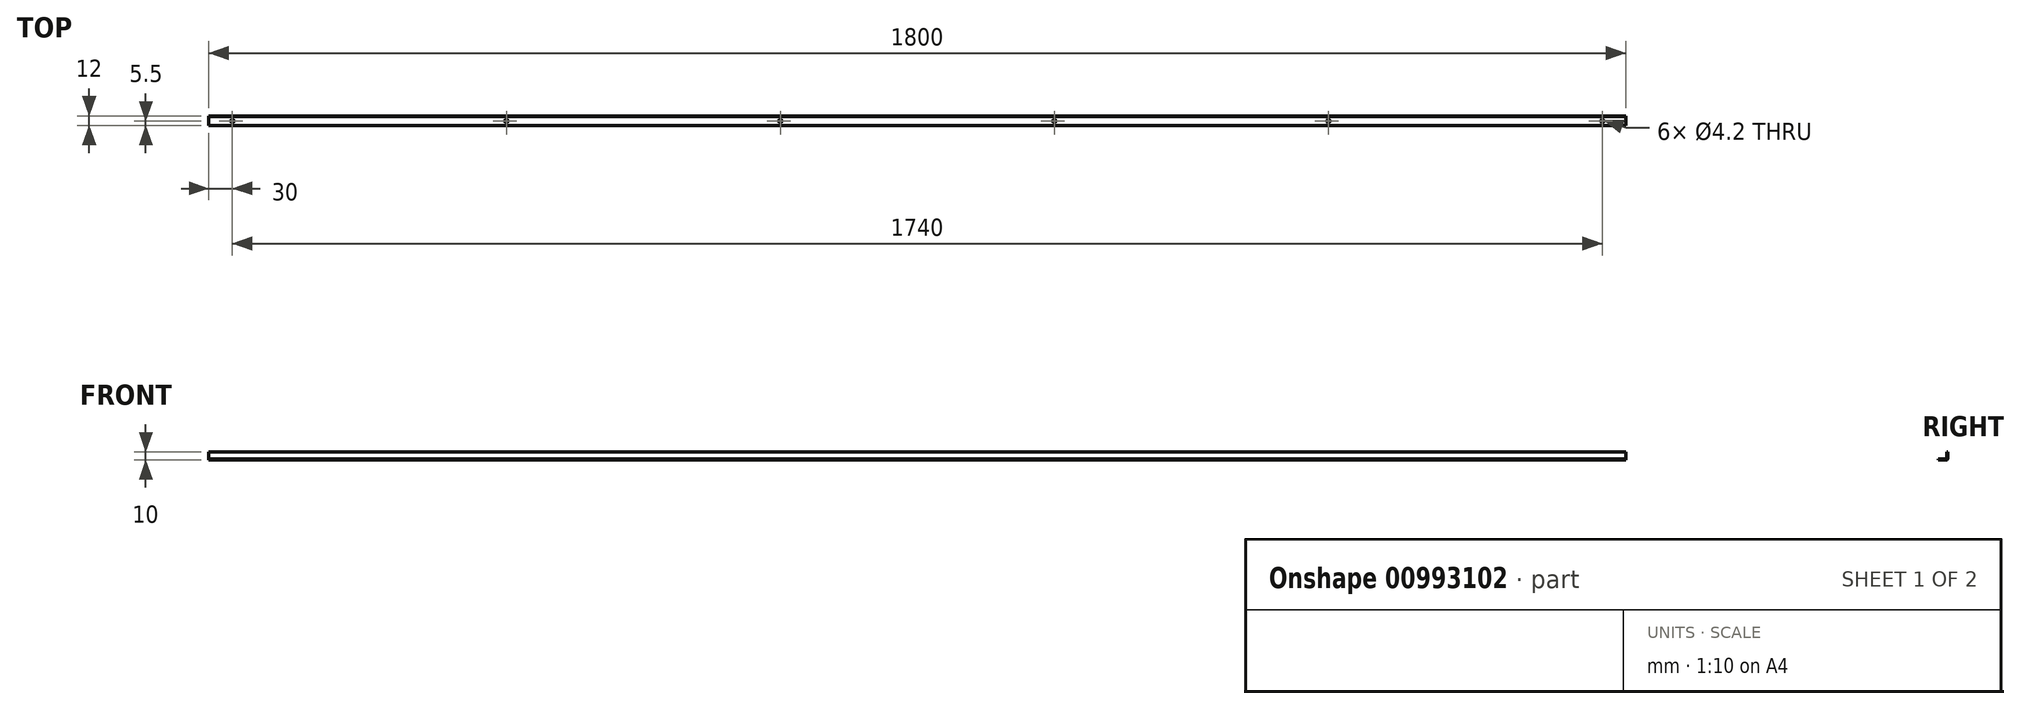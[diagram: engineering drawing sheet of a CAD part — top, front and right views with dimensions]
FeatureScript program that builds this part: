
annotation { "Feature Type Name" : "Feature", "Feature Type Description" : "" }
export const myFeature = defineFeature(function(context is Context, id is Id, definition is map)
    precondition{}
    {
        {
            var Q0;
            Q0=qCreatedBy(makeId("Right.planeOp"),FACE);
            var sketch = newSketch(context, id + "F0", { "sketchPlane" : qUnion([Q0])});
            skLineSegment(sketch, "E0", {"start": v(0, 0) * mm, "end": v(0, 10) * mm});
            skLineSegment(sketch, "E1", {"start": v(0, 10) * mm, "end": v(-1, 10) * mm});
            skLineSegment(sketch, "E2", {"start": v(-1, 10) * mm, "end": v(-1, 1) * mm});
            skLineSegment(sketch, "E3", {"start": v(-1, 1) * mm, "end": v(-12, 1) * mm});
            skLineSegment(sketch, "E4", {"start": v(-12, 1) * mm, "end": v(-12, 0) * mm});
            skLineSegment(sketch, "E5", {"start": v(-12, 0) * mm, "end": v(0, 0) * mm});
            skSolve(sketch);
        }
        {
            var Q0;
            Q0 = qSketchRegion(id + "F0", true);
            extrude(context, id + "F1", {"entities" : qUnion([Q0]), "depth" : 1800 * mm, "offsetDistance" : 25 * mm});
        }
        {
            var Q0;
            Q0=makeQuery(id+"F1.opExtrude","SWEPT_EDGE",EDGE,{"disambiguationData":[OSD([sQuery(id+"F0.wireOp",EDGE,"E2"),sQuery(id+"F0.wireOp",EDGE,"E3")])]});
            fillet(context, id + "F2", {"entities" : qUnion([Q0]), "radius" : 0.5 * mm, "tangentPropagation" : true, "allowEdgeOverflow" : false});
        }
        {
            var Q0;
            Q0=makeQuery(id+"F1.opExtrude","SWEPT_EDGE",EDGE,{"disambiguationData":[OSD([sQuery(id+"F0.wireOp",EDGE,"E0"),sQuery(id+"F0.wireOp",EDGE,"E5")])]});
            fillet(context, id + "F3", {"entities" : qUnion([Q0]), "radius" : 1.5 * mm, "tangentPropagation" : true, "allowEdgeOverflow" : false});
        }
        {
            var Q0;
            Q0=qCreatedBy(makeId("Top.planeOp"),FACE);
            var sketch = newSketch(context, id + "F4", { "sketchPlane" : qUnion([Q0])});
            skLineSegment(sketch, "E6", {"start": v(-11.38, -6.5) * mm, "end": v(1824.66, -6.5) * mm, "construction": true});
            skCircle(sketch, "E7", {"center": v(30, -6.5) * mm, "radius": 2.1 * mm});
            skCircle(sketch, "E8", {"center": v(378, -6.5) * mm, "radius": 2.1 * mm});
            skCircle(sketch, "E9", {"center": v(726, -6.5) * mm, "radius": 2.1 * mm});
            skCircle(sketch, "E10", {"center": v(1074, -6.5) * mm, "radius": 2.1 * mm});
            skCircle(sketch, "E11", {"center": v(1422, -6.5) * mm, "radius": 2.1 * mm});
            skCircle(sketch, "E12", {"center": v(1770, -6.5) * mm, "radius": 2.1 * mm});
            skSolve(sketch);
        }
        {
            var Q0;
            Q0 = qSketchRegion(id + "F4", true);
            extrude(context, id + "F5", {"entities" : qUnion([Q0]), "operationType" : NewBodyOperationType.REMOVE, "depth" : 25 * mm, "offsetDistance" : 25 * mm});
        }
    });
